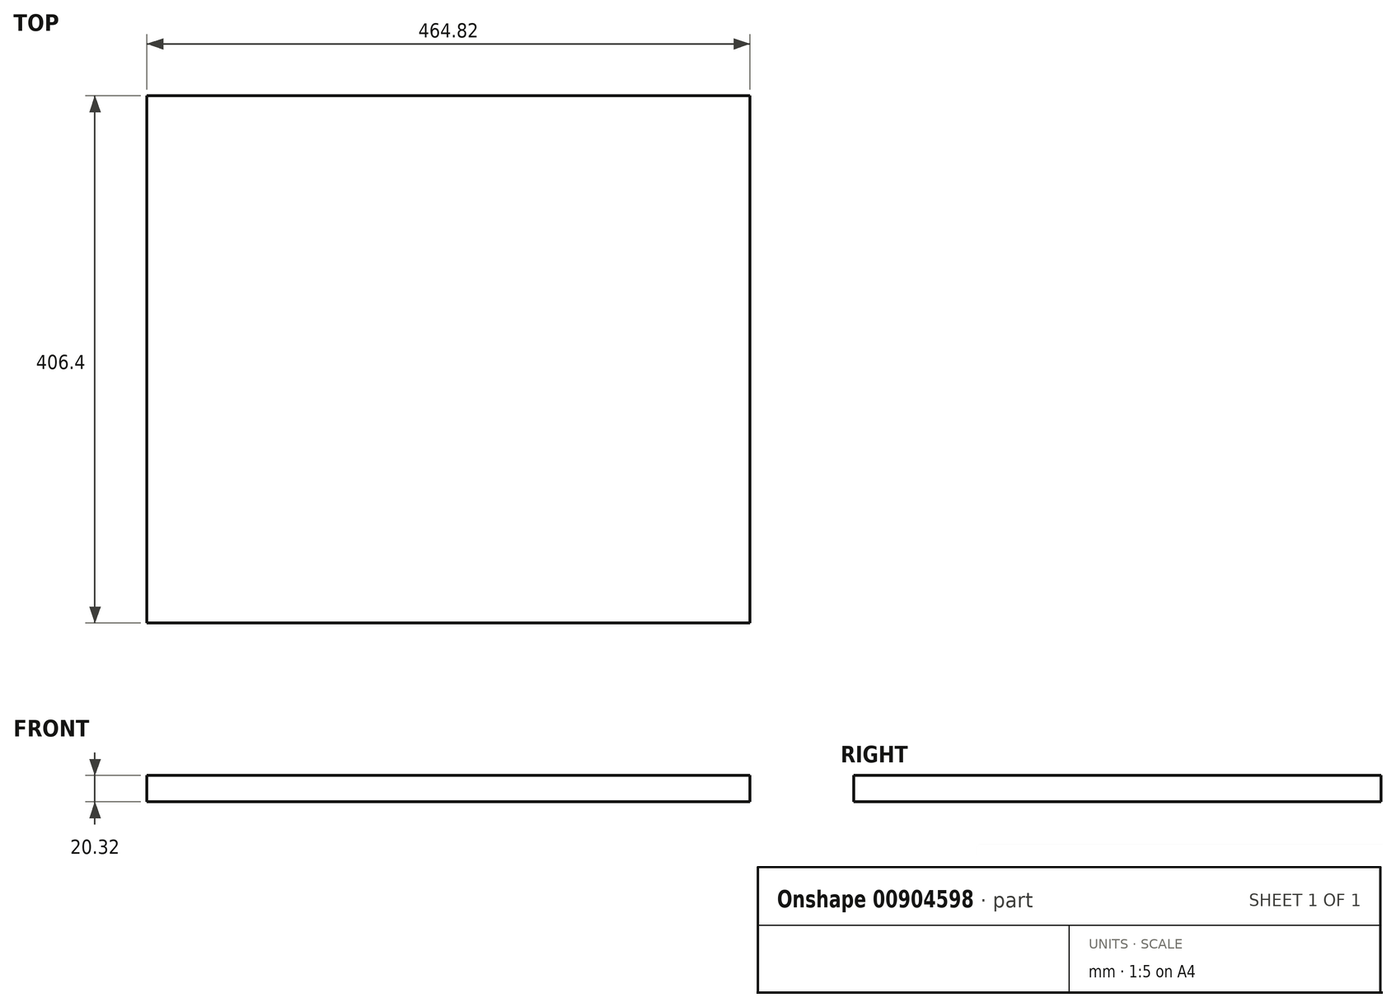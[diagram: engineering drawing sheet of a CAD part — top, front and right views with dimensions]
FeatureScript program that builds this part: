
annotation { "Feature Type Name" : "Feature", "Feature Type Description" : "" }
export const myFeature = defineFeature(function(context is Context, id is Id, definition is map)
    precondition{}
    {
        {
            var Q0;
            Q0=qCreatedBy(makeId("Top.planeOp"),FACE);
            var sketch = newSketch(context, id + "F0", { "sketchPlane" : qUnion([Q0])});
            skLineSegment(sketch, "E0.bottom", {"start": v(-30.48, -228.6) * mm, "end": v(-495.3, -228.6) * mm});
            skLineSegment(sketch, "E0.top", {"start": v(-30.48, 177.8) * mm, "end": v(-495.3, 177.8) * mm});
            skLineSegment(sketch, "E0.left", {"start": v(-30.48, -228.6) * mm, "end": v(-30.48, 177.8) * mm});
            skLineSegment(sketch, "E0.right", {"start": v(-495.3, -228.6) * mm, "end": v(-495.3, 177.8) * mm});
            skPoint(sketch, "E0.middle", {"position": v(-262.9, -25.4) * mm});
            skSolve(sketch);
        }
        {
            var Q0;
            Q0 = qSketchRegion(id + "F0", true);
            extrude(context, id + "F1", {"entities" : qUnion([Q0]), "depth" : 20.32 * mm, "offsetDistance" : 25.4 * mm});
        }
    });
